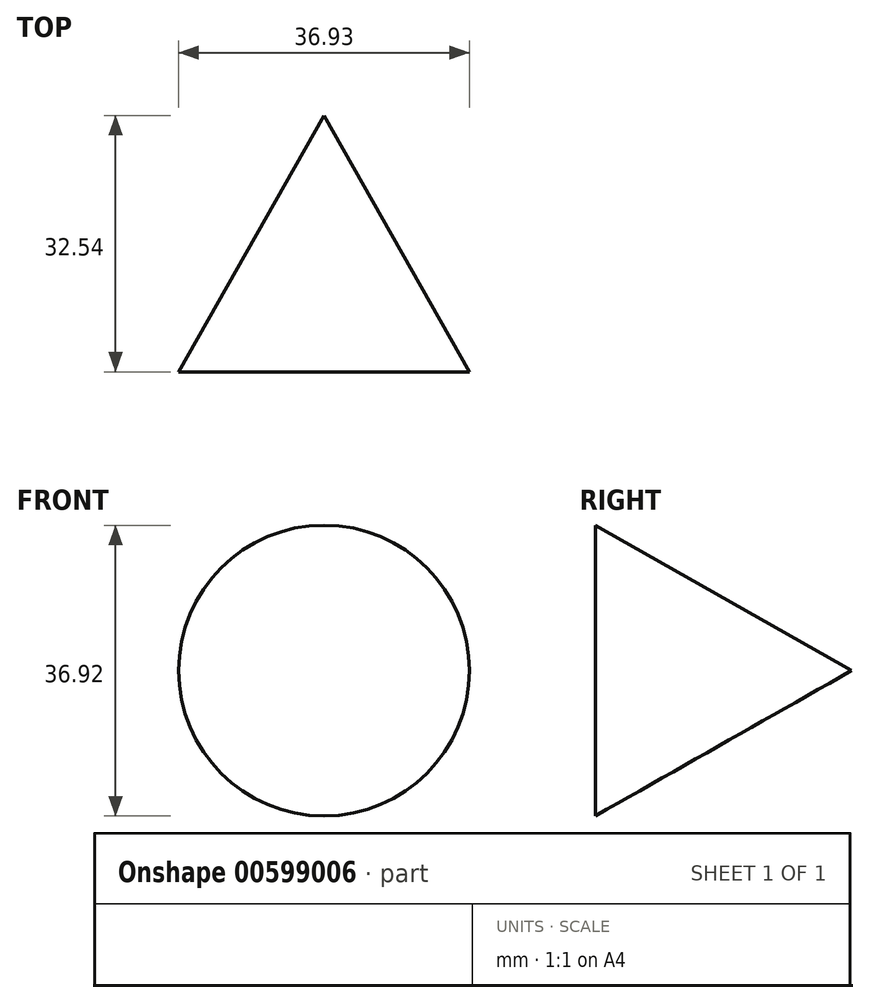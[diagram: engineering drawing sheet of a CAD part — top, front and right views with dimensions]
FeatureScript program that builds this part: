
annotation { "Feature Type Name" : "Feature", "Feature Type Description" : "" }
export const myFeature = defineFeature(function(context is Context, id is Id, definition is map)
    precondition{}
    {
        {
            var Q0;
            Q0=qCreatedBy(makeId("Top.planeOp"),FACE);
            var sketch = newSketch(context, id + "F0", { "sketchPlane" : qUnion([Q0])});
            skLineSegment(sketch, "E0", {"start": v(-17.43, 52.1) * mm, "end": v(-35.9, 19.55) * mm});
            skLineSegment(sketch, "E1", {"start": v(-35.9, 19.55) * mm, "end": v(-17.43, 19.55) * mm});
            skLineSegment(sketch, "E2", {"start": v(-17.43, 19.55) * mm, "end": v(-17.43, 52.1) * mm});
            skSolve(sketch);
        }
        {
            var Q0;
            Q0=makeQuery(id+"F0.imprint","IMPRINT",FACE,{"disambiguationData":[TD([[makeQuery(id+"F0.imprint","IMPRINT",EDGE,{"derivedFrom":sQuery(id+"F0.wireOp",EDGE,"E0")}),1.0]])]});
            var Q1;
            Q1=sQuery(id+"F0.wireOp",EDGE,"E2");
            revolve(context, id + "F1", {"entities" : qUnion([Q0]), "axis" : qUnion([Q1]), "revolveType" : RevolveType.FULL});
        }
    });
